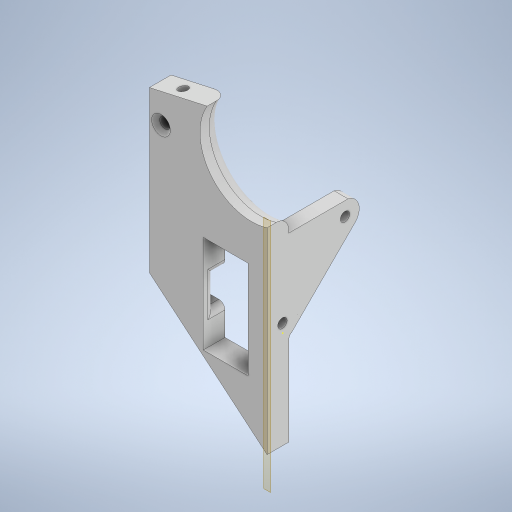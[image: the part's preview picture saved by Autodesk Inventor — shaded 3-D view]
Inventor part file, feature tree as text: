
AUTODESK INVENTOR PART (.ipt)
format: ipt  version: 2023 (Build 270158000, 158)  size: 574,976 bytes
history: native  units: in
note: dims shown in document units (in); Inventor stores cm internally (conversion verified against a paired STEP export)
features: sketch x28, extrude x10, other x9, projected_geometry x9, reference x8, fillet x3, hole x2
ambient origin geometry x8: Origin, YZ Plane, XZ Plane, XY Plane, X Axis, Y Axis, Z Axis, Center Point
bodies: Body1 (feature_tree), Body2 (feature_tree), Body3 (feature_tree)
feature tree (69):
  other  "SCIANA_2.0_MIR.ipt"
  extrude  "Wyciągnięcie proste1"  Depth=0.3937in
  extrude  "Wyciągnięcie proste2"  Depth=0.1772in TaperAngle=0.0deg
  sketch  "Szkic20"
  sketch  "Szkic21"
  extrude  "Wyciągnięcie proste3"  Depth=0.315in TaperAngle=0.0deg
  extrude  "Wyciągnięcie proste4"  Depth=0.315in TaperAngle=0.0deg
  extrude  "Wyciągnięcie proste5"  Depth=0.3937in TaperAngle=0.0deg
  sketch  "Szkic23"
  extrude  "Wyciągnięcie proste6"  TaperAngle=0.0deg  [1 undecoded]
  extrude  "Wyciągnięcie proste7"  Depth=0.3937in TaperAngle=0.0deg
  extrude  "Wyciągnięcie proste8"  Depth=0.3937in TaperAngle=0.0deg
  fillet  "Zaokrąglenie1"  Radius=0.2165in
  fillet  "Zaokrąglenie2"  Radius=0.0827in
  extrude  "Wyciągnięcie proste9"  Depth=0.0787in
  fillet  "Zaokrąglenie4"  Radius=0.0787in
  hole  "Otwór2"  [1 undecoded]
  hole  "Otwór3"  [1 undecoded]
  extrude  "Wyciągnięcie proste10"  Depth=0.2992in
  other  "Bryła1::SCIANA_2.0_MIR.ipt"
  other  "Bryła wyprowadzona1"
  sketch  "Szkic1"
  sketch  "Szkic2"
  sketch  "Szkic3"
  sketch  "Szkic4"
  sketch  "Szkic5"
  sketch  "Szkic6"
  sketch  "Szkic7"
  sketch  "Szkic8"
  sketch  "Szkic9"
  sketch  "Szkic10"
  sketch  "Szkic11"
  sketch  "Szkic12"
  sketch  "Szkic13"
  sketch  "Szkic14"
  sketch  "Szkic15"
  sketch  "Szkic16"
  sketch  "Szkic17"
  other  "Płaszczyzna konstrukcyjna1"
  other  "Płaszczyzna konstrukcyjna2"
  sketch  "Szkic18"
  reference  "Odniesienie1"
  reference  "Odniesienie2"
  projected_geometry  "Pętla rzutowana1"
  reference  "Odniesienie3"
  reference  "Odniesienie4"
  reference  "Odniesienie5"
  reference  "Odniesienie6"
  reference  "Odniesienie7"
  sketch  "Szkic19"
  reference  "Odniesienie8"
  projected_geometry  "Pętla rzutowana2"
  sketch  "Szkic22"
  projected_geometry  "Pętla rzutowana3"
  projected_geometry  "Pętla rzutowana4"
  sketch  "Szkic24"
  projected_geometry  "Pętla rzutowana5"
  sketch  "Szkic26"
  projected_geometry  "Pętla rzutowana7"
  sketch  "Szkic27"
  projected_geometry  "Pętla rzutowana8"
  sketch  "Szkic28"
  projected_geometry  "Pętla rzutowana9"
  sketch  "Szkic29"
  projected_geometry  "Pętla rzutowana10"
  other  "Bryła1"
  other  "<userpath>\Desktop\MojeRoboty\Stefan\mechanics\Zespół1.iam"
  other  "Zespół1.iam"
  other  "sciana_prawa_v4:1"
note: 3 required parameter values undecoded (feature->parameter linkage not recoverable at this tier; creation-order binding heuristic only, values carry confidence <= 0.55)
